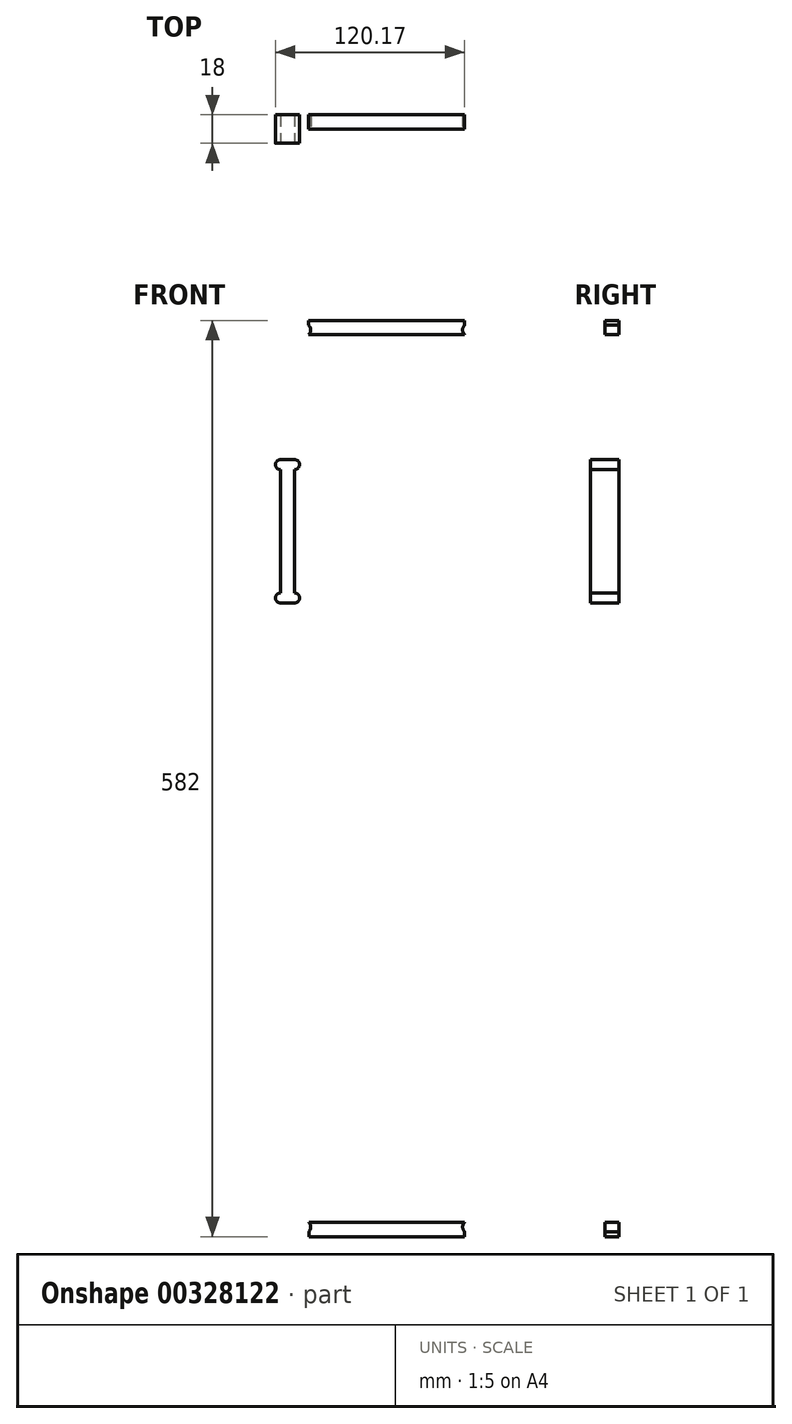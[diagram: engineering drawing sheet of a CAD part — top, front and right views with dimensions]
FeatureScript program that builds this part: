
annotation { "Feature Type Name" : "Feature", "Feature Type Description" : "" }
export const myFeature = defineFeature(function(context is Context, id is Id, definition is map)
    precondition{}
    {
        {
            var Q0;
            Q0=qCreatedBy(makeId("Front.planeOp"),FACE);
            var sketch = newSketch(context, id + "F0", { "sketchPlane" : qUnion([Q0])});
            skArc(sketch, "E0", {"start": v(28.2, 509.55) * mm, "mid": v(31.37, 506.37) * mm, "end": v(28.2, 503.2) * mm});
            skLineSegment(sketch, "E1", {"start": v(28.2, 503.2) * mm, "end": v(28.2, 424.9) * mm});
            skArc(sketch, "E2", {"start": v(28.2, 424.9) * mm, "mid": v(31.37, 421.72) * mm, "end": v(28.2, 418.55) * mm});
            skLineSegment(sketch, "E3", {"start": v(28.2, 418.55) * mm, "end": v(19.2, 418.55) * mm});
            skArc(sketch, "E4", {"start": v(19.2, 418.55) * mm, "mid": v(16.02, 421.72) * mm, "end": v(19.2, 424.9) * mm});
            skLineSegment(sketch, "E5", {"start": v(19.2, 424.9) * mm, "end": v(19.2, 503.2) * mm});
            skArc(sketch, "E6", {"start": v(19.2, 503.2) * mm, "mid": v(16.02, 506.37) * mm, "end": v(19.2, 509.55) * mm});
            skLineSegment(sketch, "E7", {"start": v(19.2, 509.55) * mm, "end": v(28.2, 509.55) * mm});
            skLineSegment(sketch, "E8", {"start": v(28.2, 104.55) * mm, "end": v(19.2, 104.55) * mm});
            skArc(sketch, "E9", {"start": v(19.2, 104.55) * mm, "mid": v(16.02, 107.72) * mm, "end": v(19.2, 110.9) * mm});
            skLineSegment(sketch, "E10", {"start": v(19.2, 110.9) * mm, "end": v(19.2, 189.2) * mm});
            skArc(sketch, "E11", {"start": v(19.2, 189.2) * mm, "mid": v(16.02, 192.37) * mm, "end": v(19.2, 195.55) * mm});
            skLineSegment(sketch, "E12", {"start": v(19.2, 195.55) * mm, "end": v(28.2, 195.55) * mm});
            skArc(sketch, "E13", {"start": v(28.2, 195.55) * mm, "mid": v(31.37, 192.38) * mm, "end": v(28.2, 189.2) * mm});
            skLineSegment(sketch, "E14", {"start": v(28.2, 189.2) * mm, "end": v(28.2, 110.9) * mm});
            skArc(sketch, "E15", {"start": v(28.2, 110.9) * mm, "mid": v(31.37, 107.72) * mm, "end": v(28.2, 104.55) * mm});
            skLineSegment(sketch, "E16", {"start": v(141.66, 25.05) * mm, "end": v(163.16, 25.05) * mm});
            skLineSegment(sketch, "E17", {"start": v(163.16, 25.05) * mm, "end": v(163.16, 589.05) * mm});
            skLineSegment(sketch, "E18", {"start": v(163.16, 589.05) * mm, "end": v(141.64, 589.05) * mm});
            skArc(sketch, "E19", {"start": v(141.64, 589.05) * mm, "mid": v(135.98, 589.24) * mm, "end": v(136.17, 594.89) * mm});
            skLineSegment(sketch, "E20", {"start": v(136.17, 594.89) * mm, "end": v(136.17, 598.05) * mm});
            skLineSegment(sketch, "E21", {"start": v(136.17, 598.05) * mm, "end": v(37.17, 598.05) * mm});
            skLineSegment(sketch, "E22", {"start": v(37.17, 598.05) * mm, "end": v(37.17, 594.89) * mm});
            skArc(sketch, "E23", {"start": v(37.17, 594.89) * mm, "mid": v(37.35, 589.23) * mm, "end": v(31.7, 589.05) * mm});
            skLineSegment(sketch, "E24", {"start": v(31.7, 589.05) * mm, "end": v(10.2, 589.05) * mm});
            skLineSegment(sketch, "E25", {"start": v(10.2, 589.05) * mm, "end": v(10.2, 25.05) * mm});
            skLineSegment(sketch, "E26", {"start": v(10.2, 25.05) * mm, "end": v(31.73, 25.05) * mm});
            skArc(sketch, "E27", {"start": v(31.73, 25.05) * mm, "mid": v(37.38, 24.86) * mm, "end": v(37.2, 19.21) * mm});
            skLineSegment(sketch, "E28", {"start": v(37.2, 19.21) * mm, "end": v(37.2, 16.05) * mm});
            skLineSegment(sketch, "E29", {"start": v(37.2, 16.05) * mm, "end": v(136.2, 16.05) * mm});
            skLineSegment(sketch, "E30", {"start": v(136.2, 16.05) * mm, "end": v(136.2, 19.21) * mm});
            skArc(sketch, "E31", {"start": v(136.2, 19.21) * mm, "mid": v(136, 24.86) * mm, "end": v(141.66, 25.05) * mm});
            skLineSegment(sketch, "E32", {"start": v(146.2, 21.05) * mm, "end": v(146.2, 10.05) * mm});
            skArc(sketch, "E33", {"start": v(146.2, 10.05) * mm, "mid": v(145.02, 7.22) * mm, "end": v(142.2, 6.05) * mm});
            skLineSegment(sketch, "E34", {"start": v(142.2, 6.05) * mm, "end": v(31.2, 6.05) * mm});
            skArc(sketch, "E35", {"start": v(31.2, 6.05) * mm, "mid": v(28.37, 7.22) * mm, "end": v(27.2, 10.05) * mm});
            skLineSegment(sketch, "E36", {"start": v(27.2, 10.05) * mm, "end": v(27.2, 21.05) * mm});
            skArc(sketch, "E37", {"start": v(27.2, 21.05) * mm, "mid": v(28.37, 23.88) * mm, "end": v(31.2, 25.05) * mm});
            skLineSegment(sketch, "E38", {"start": v(31.2, 25.05) * mm, "end": v(37.2, 25.05) * mm});
            skLineSegment(sketch, "E39", {"start": v(37.2, 25.05) * mm, "end": v(136.2, 25.05) * mm});
            skLineSegment(sketch, "E40", {"start": v(136.2, 25.05) * mm, "end": v(142.2, 25.05) * mm});
            skArc(sketch, "E41", {"start": v(142.2, 25.05) * mm, "mid": v(145.02, 23.88) * mm, "end": v(146.2, 21.05) * mm});
            skArc(sketch, "E42", {"start": v(27.17, 593.05) * mm, "mid": v(28.34, 590.22) * mm, "end": v(31.17, 589.05) * mm});
            skLineSegment(sketch, "E43", {"start": v(31.17, 589.05) * mm, "end": v(37.17, 589.05) * mm});
            skLineSegment(sketch, "E44", {"start": v(37.17, 589.05) * mm, "end": v(136.17, 589.05) * mm});
            skLineSegment(sketch, "E45", {"start": v(136.17, 589.05) * mm, "end": v(142.17, 589.05) * mm});
            skArc(sketch, "E46", {"start": v(142.17, 589.05) * mm, "mid": v(145, 590.22) * mm, "end": v(146.17, 593.05) * mm});
            skLineSegment(sketch, "E47", {"start": v(146.17, 593.05) * mm, "end": v(146.17, 604.05) * mm});
            skArc(sketch, "E48", {"start": v(146.17, 604.05) * mm, "mid": v(145, 606.88) * mm, "end": v(142.17, 608.05) * mm});
            skLineSegment(sketch, "E49", {"start": v(142.17, 608.05) * mm, "end": v(31.17, 608.04) * mm});
            skArc(sketch, "E50", {"start": v(31.17, 608.04) * mm, "mid": v(28.34, 606.87) * mm, "end": v(27.17, 604.04) * mm});
            skLineSegment(sketch, "E51", {"start": v(27.17, 604.04) * mm, "end": v(27.17, 593.05) * mm});
            skSolve(sketch);
        }
        {
            var Q0;
            {var subQ2=sQuery(id+"F0.wireOp",EDGE,"E28");Q0=makeQuery(id+"F0.imprint","IMPRINT",FACE,{"disambiguationData":[TD([[makeQuery(id+"F0.imprint","IMPRINT",EDGE,{"derivedFrom":subQ2}),1.0]])]});}
            var Q1;
            {var subQ1=sQuery(id+"F0.wireOp",EDGE,"E20");Q1=makeQuery(id+"F0.imprint","IMPRINT",FACE,{"disambiguationData":[TD([[makeQuery(id+"F0.imprint","IMPRINT",EDGE,{"derivedFrom":subQ1}),1.0]])]});}
            var Q2;
            Q2=makeQuery(id+"F0.imprint","IMPRINT",FACE,{"disambiguationData":[TD([[makeQuery(id+"F0.imprint","IMPRINT",EDGE,{"derivedFrom":sQuery(id+"F0.wireOp",EDGE,"E0")}),1.0]])]});
            extrude(context, id + "F1", {"entities" : qUnion([Q0, Q1, Q2]), "oppositeDirection" : true, "depth" : 18 * mm});
        }
        {
            var Q0;
            Q0=makeQuery(id+"F0.imprint","IMPRINT",FACE,{"disambiguationData":[TD([[makeQuery(id+"F0.imprint","IMPRINT",EDGE,{"derivedFrom":sQuery(id+"F0.wireOp",EDGE,"E8")}),-1.0]])]});
            var Q1;
            Q1=makeQuery(id+"F0.imprint","IMPRINT",FACE,{"disambiguationData":[TD([[makeQuery(id+"F0.imprint","IMPRINT",EDGE,{"derivedFrom":sQuery(id+"F0.wireOp",EDGE,"E0")}),-1.0]])]});
            var Q2;
            {var subQ2=sQuery(id+"F0.wireOp",EDGE,"E28");Q2=makeQuery(id+"F0.imprint","IMPRINT",FACE,{"disambiguationData":[TD([[makeQuery(id+"F0.imprint","IMPRINT",EDGE,{"derivedFrom":subQ2}),1.0]])]});}
            var Q3;
            {var subQ1=sQuery(id+"F0.wireOp",EDGE,"E20");Q3=makeQuery(id+"F0.imprint","IMPRINT",FACE,{"disambiguationData":[TD([[makeQuery(id+"F0.imprint","IMPRINT",EDGE,{"derivedFrom":subQ1}),1.0]])]});}
            extrude(context, id + "F2", {"entities" : qUnion([Q0, Q1, Q2, Q3]), "operationType" : NewBodyOperationType.REMOVE, "oppositeDirection" : true, "depth" : 9 * mm});
        }
    });
